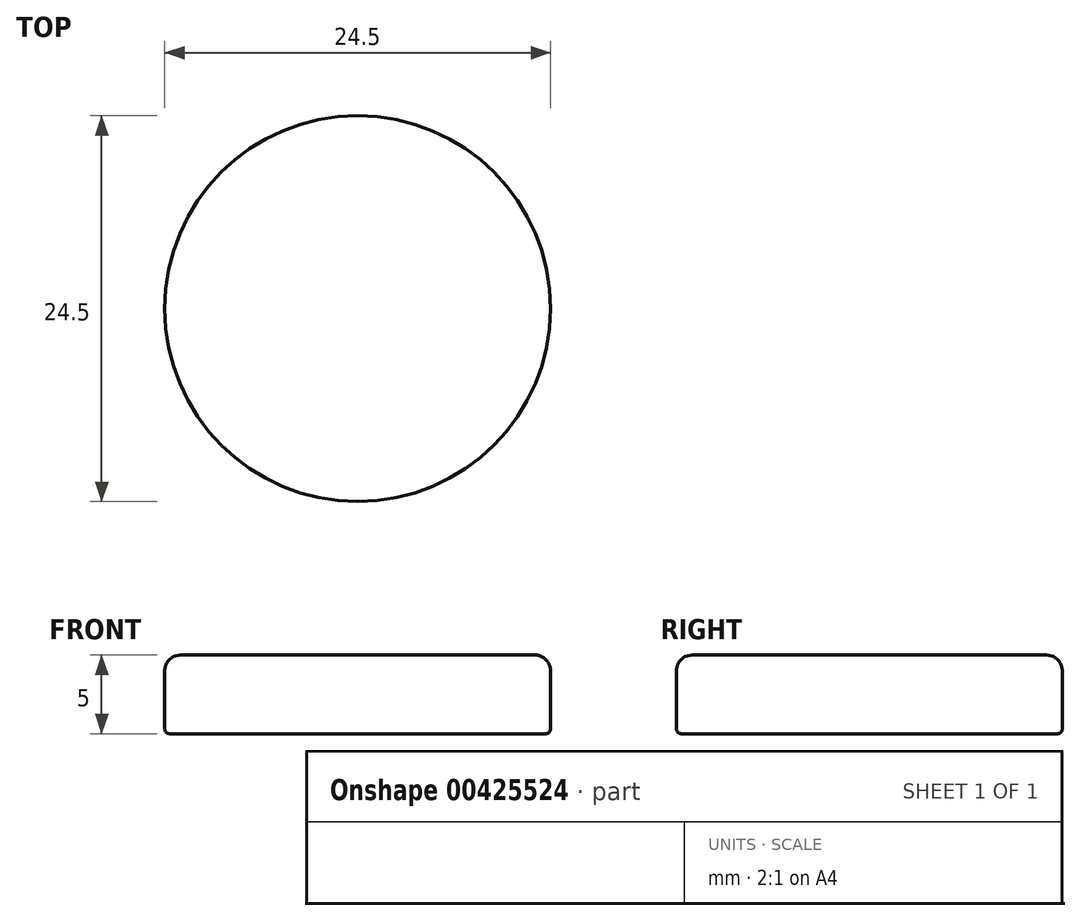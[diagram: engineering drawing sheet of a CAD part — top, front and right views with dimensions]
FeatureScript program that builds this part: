
annotation { "Feature Type Name" : "Feature", "Feature Type Description" : "" }
export const myFeature = defineFeature(function(context is Context, id is Id, definition is map)
    precondition{}
    {
        {
            var Q0;
            Q0=qCreatedBy(makeId("Top.planeOp"),FACE);
            var sketch = newSketch(context, id + "F0", { "sketchPlane" : qUnion([Q0])});
            skCircle(sketch, "E0", {"center": v(0, 0) * mm, "radius": 12.25 * mm});
            skSolve(sketch);
        }
        {
            var Q0;
            Q0 = qSketchRegion(id + "F0", true);
            extrude(context, id + "F1", {"entities" : qUnion([Q0]), "depth" : 5 * mm});
        }
        {
            var Q0;
            Q0=makeQuery(id+"F1.opExtrude","CAP_EDGE",EDGE,{"disambiguationData":[OSD([sQuery(id+"F0.wireOp",EDGE,"E0")])],"isStart":false});
            fillet(context, id + "F2", {"entities" : qUnion([Q0]), "radius" : 1 * mm, "tangentPropagation" : true, "allowEdgeOverflow" : false});
        }
        {
            var Q0;
            Q0=makeQuery(id+"F1.opExtrude","CAP_EDGE",EDGE,{"disambiguationData":[OSD([sQuery(id+"F0.wireOp",EDGE,"E0")])],"isStart":true});
            fillet(context, id + "F3", {"entities" : qUnion([Q0]), "radius" : .3 * mm, "tangentPropagation" : true, "allowEdgeOverflow" : false});
        }
    });
